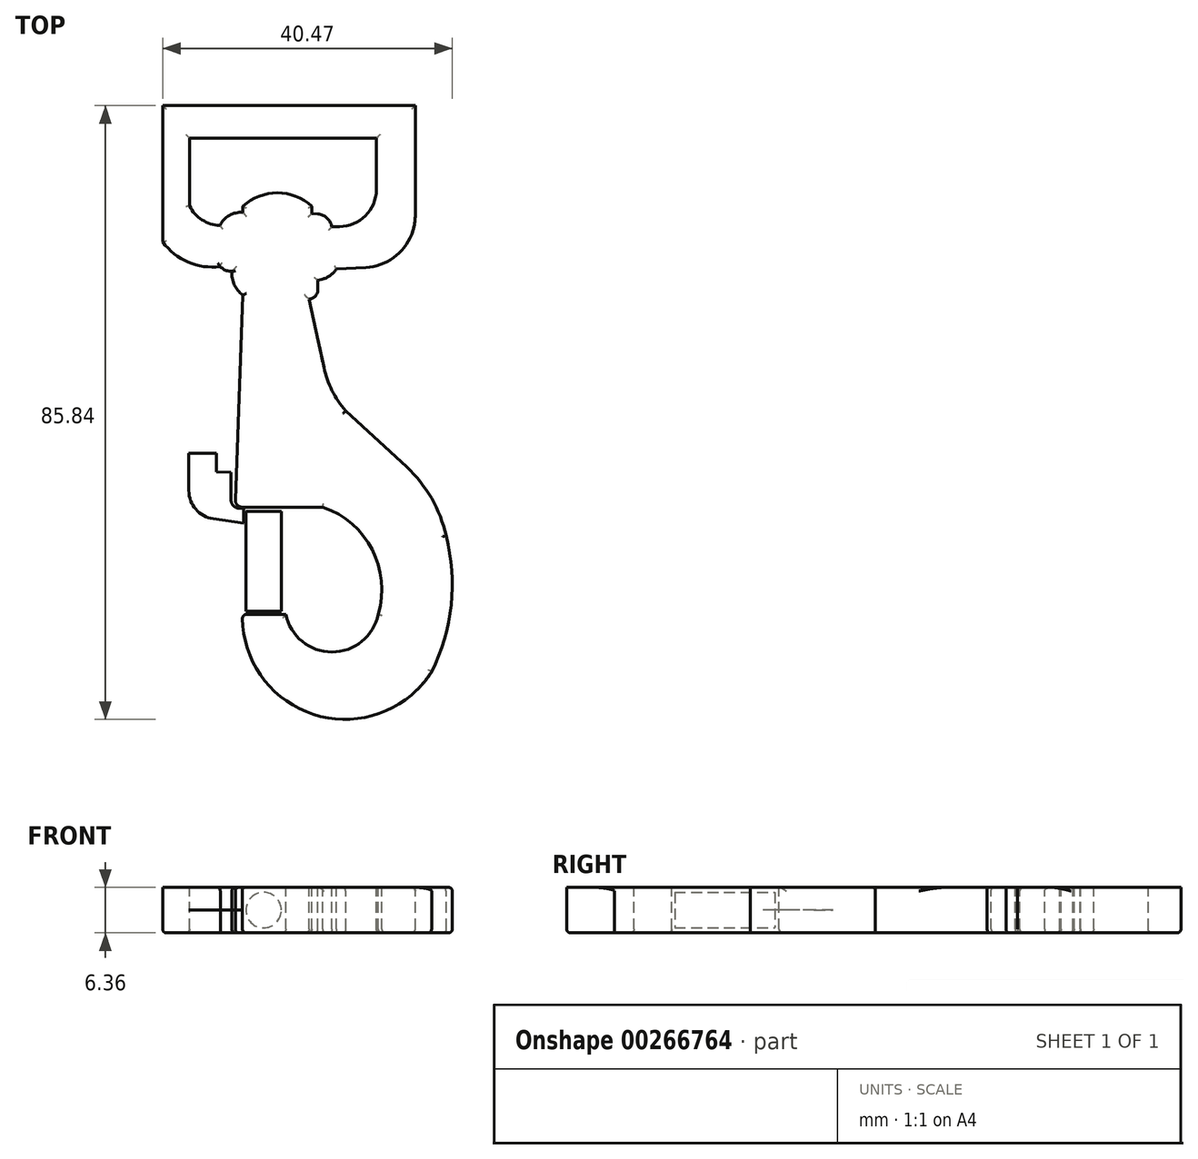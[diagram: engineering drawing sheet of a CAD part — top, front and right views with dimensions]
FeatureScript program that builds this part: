
annotation { "Feature Type Name" : "Feature", "Feature Type Description" : "" }
export const myFeature = defineFeature(function(context is Context, id is Id, definition is map)
    precondition{}
    {
        {
            var Q0;
            Q0=qCreatedBy(makeId("Top.planeOp"),FACE);
            var sketch = newSketch(context, id + "F0", { "sketchPlane" : qUnion([Q0])});
            skLineSegment(sketch, "E0", {"start": v(0, 0) * mm, "end": v(35.3, 0) * mm});
            skLineSegment(sketch, "E1", {"start": v(35.3, 0) * mm, "end": v(35.3, -15.36) * mm});
            skArc(sketch, "E2", {"start": v(28.4, -22.64) * mm, "mid": v(33.3, -20.38) * mm, "end": v(35.3, -15.36) * mm});
            skLineSegment(sketch, "E3", {"start": v(28.4, -22.64) * mm, "end": v(24.3, -22.86) * mm});
            skArc(sketch, "E4", {"start": v(22.26, -24.3) * mm, "mid": v(23.41, -23.76) * mm, "end": v(24.3, -22.86) * mm});
            skLineSegment(sketch, "E5", {"start": v(22.26, -24.3) * mm, "end": v(21.7, -24.44) * mm});
            skLineSegment(sketch, "E6", {"start": v(21.7, -24.44) * mm, "end": v(21.7, -25.7) * mm});
            skArc(sketch, "E7", {"start": v(20.5, -27.08) * mm, "mid": v(21.36, -26.62) * mm, "end": v(21.7, -25.7) * mm});
            skLineSegment(sketch, "E8", {"start": v(20.5, -27.08) * mm, "end": v(22.54, -36.62) * mm});
            skArc(sketch, "E9", {"start": v(22.54, -36.62) * mm, "mid": v(23.67, -39.85) * mm, "end": v(25.58, -42.7) * mm});
            skLineSegment(sketch, "E10", {"start": v(25.58, -42.7) * mm, "end": v(34.09, -50.55) * mm});
            skArc(sketch, "E11", {"start": v(39.62, -60.16) * mm, "mid": v(37.59, -54.93) * mm, "end": v(34.09, -50.55) * mm});
            skArc(sketch, "E12", {"start": v(37.58, -79.19) * mm, "mid": v(40.32, -69.85) * mm, "end": v(39.62, -60.16) * mm});
            skArc(sketch, "E13", {"start": v(11.15, -71.74) * mm, "mid": v(21.6, -85.3) * mm, "end": v(37.58, -79.19) * mm});
            skArc(sketch, "E14", {"start": v(11.74, -71.15) * mm, "mid": v(11.32, -71.32) * mm, "end": v(11.15, -71.74) * mm});
            skLineSegment(sketch, "E15", {"start": v(11.74, -71.15) * mm, "end": v(17.2, -71.15) * mm});
            skArc(sketch, "E16", {"start": v(17.2, -71.15) * mm, "mid": v(23.66, -76.42) * mm, "end": v(30.12, -71.15) * mm});
            skArc(sketch, "E17", {"start": v(30.12, -71.15) * mm, "mid": v(29.28, -62.1) * mm, "end": v(22.4, -56.16) * mm});
            skLineSegment(sketch, "E18", {"start": v(22.4, -56.16) * mm, "end": v(11.12, -56.16) * mm});
            skArc(sketch, "E19", {"start": v(10.17, -55.17) * mm, "mid": v(10.43, -55.87) * mm, "end": v(11.12, -56.16) * mm});
            skLineSegment(sketch, "E20", {"start": v(10.17, -55.17) * mm, "end": v(11.2, -26.51) * mm});
            skArc(sketch, "E21", {"start": v(9.68, -23.18) * mm, "mid": v(10.01, -25.04) * mm, "end": v(11.2, -26.51) * mm});
            skArc(sketch, "E22", {"start": v(8.05, -22.5) * mm, "mid": v(8.8, -23.02) * mm, "end": v(9.68, -23.18) * mm});
            skArc(sketch, "E23", {"start": v(0, -19.06) * mm, "mid": v(3.56, -21.88) * mm, "end": v(8.05, -22.5) * mm});
            skLineSegment(sketch, "E24", {"start": v(0, -19.06) * mm, "end": v(0, 0) * mm});
            skLineSegment(sketch, "E25", {"start": v(9.56, -51.3) * mm, "end": v(7.52, -51.22) * mm});
            skLineSegment(sketch, "E26", {"start": v(7.52, -51.22) * mm, "end": v(7.52, -48.65) * mm});
            skLineSegment(sketch, "E27", {"start": v(7.52, -48.65) * mm, "end": v(3.66, -48.65) * mm});
            skLineSegment(sketch, "E28", {"start": v(3.66, -48.65) * mm, "end": v(3.66, -53.86) * mm});
            skArc(sketch, "E29", {"start": v(3.66, -53.86) * mm, "mid": v(4.63, -56.45) * mm, "end": v(7.07, -57.78) * mm});
            skLineSegment(sketch, "E30", {"start": v(7.07, -57.78) * mm, "end": v(11.35, -58.39) * mm});
            skLineSegment(sketch, "E31", {"start": v(9.56, -51.3) * mm, "end": v(9.56, -55.14) * mm});
            skArc(sketch, "E32", {"start": v(9.56, -55.14) * mm, "mid": v(9.92, -56) * mm, "end": v(10.78, -56.33) * mm});
            skLineSegment(sketch, "E33", {"start": v(10.78, -56.33) * mm, "end": v(11.35, -56.32) * mm});
            skLineSegment(sketch, "E34", {"start": v(11.35, -56.32) * mm, "end": v(11.35, -58.39) * mm});
            skLineSegment(sketch, "E35", {"start": v(3.77, -4.56) * mm, "end": v(29.87, -4.56) * mm});
            skLineSegment(sketch, "E36", {"start": v(29.87, -4.56) * mm, "end": v(29.87, -11.74) * mm});
            skArc(sketch, "E37", {"start": v(24.7, -16.91) * mm, "mid": v(28.36, -15.4) * mm, "end": v(29.87, -11.74) * mm});
            skLineSegment(sketch, "E38", {"start": v(24.7, -16.91) * mm, "end": v(23.65, -16.91) * mm});
            skArc(sketch, "E39", {"start": v(23.65, -16.91) * mm, "mid": v(22.97, -15.71) * mm, "end": v(21.7, -15.16) * mm});
            skLineSegment(sketch, "E40", {"start": v(21.7, -15.16) * mm, "end": v(20.86, -15.08) * mm});
            skLineSegment(sketch, "E41", {"start": v(20.86, -15.08) * mm, "end": v(20.86, -14.1) * mm});
            skArc(sketch, "E42", {"start": v(20.86, -14.1) * mm, "mid": v(16.03, -12.2) * mm, "end": v(11.21, -14.1) * mm});
            skLineSegment(sketch, "E43", {"start": v(11.21, -14.1) * mm, "end": v(11.21, -14.94) * mm});
            skArc(sketch, "E44", {"start": v(11.21, -14.94) * mm, "mid": v(9.33, -15.34) * mm, "end": v(8, -16.74) * mm});
            skArc(sketch, "E45", {"start": v(3.77, -14.02) * mm, "mid": v(5.5, -15.97) * mm, "end": v(8, -16.74) * mm});
            skLineSegment(sketch, "E46", {"start": v(3.77, -4.56) * mm, "end": v(3.77, -14.02) * mm});
            skSolve(sketch);
        }
        {
            var Q0;
            Q0=makeQuery(id+"F0.imprint","IMPRINT",FACE,{"disambiguationData":[TD([[makeQuery(id+"F0.imprint","IMPRINT",EDGE,{"derivedFrom":sQuery(id+"F0.wireOp",EDGE,"E0")}),-1.0]])]});
            extrude(context, id + "F1", {"entities" : qUnion([Q0]), "endBound" : BoundingType.SYMMETRIC, "oppositeDirection" : true, "depth" : 6.35 * mm});
        }
        {
            var Q0;
            Q0=makeQuery(id+"F0.imprint","IMPRINT",FACE,{"disambiguationData":[TD([[makeQuery(id+"F0.imprint","IMPRINT",EDGE,{"derivedFrom":sQuery(id+"F0.wireOp",EDGE,"E25")}),1.0]])]});
            extrude(context, id + "F2", {"entities" : qUnion([Q0]), "oppositeDirection" : true, "depth" : 1 / 203.2 * mm});
        }
        {
            var Q0;
            Q0=qCreatedBy(makeId("Top.planeOp"),FACE);
            var sketch = newSketch(context, id + "F3", { "sketchPlane" : qUnion([Q0])});
            skLineSegment(sketch, "E47.bottom", {"start": v(14.1, -56.78) * mm, "end": v(16.59, -56.78) * mm});
            skLineSegment(sketch, "E47.top", {"start": v(14.1, -70.74) * mm, "end": v(16.59, -70.74) * mm});
            skLineSegment(sketch, "E47.left", {"start": v(14.1, -56.78) * mm, "end": v(14.1, -70.74) * mm});
            skLineSegment(sketch, "E47.right", {"start": v(16.59, -56.78) * mm, "end": v(16.59, -70.74) * mm});
            skSolve(sketch);
        }
        {
            var Q0;
            Q0=makeQuery(id+"F0.imprint","IMPRINT",FACE,{"disambiguationData":[TD([[makeQuery(id+"F0.imprint","IMPRINT",EDGE,{"derivedFrom":sQuery(id+"F0.wireOp",EDGE,"E35")}),-1.0]])]});
            extrude(context, id + "F4", {"entities" : qUnion([Q0]), "operationType" : NewBodyOperationType.REMOVE, "oppositeDirection" : true, "depth" : 25.4 * mm});
        }
        {
            var Q0;
            Q0=makeQuery(id+"F1.opExtrude","CAP_EDGE",EDGE,{"disambiguationData":[OSD([sQuery(id+"F0.wireOp",EDGE,"E20")])],"isStart":true});
            var Q1;
            Q1=makeQuery(id+"F1.opExtrude","CAP_EDGE",EDGE,{"disambiguationData":[OSD([sQuery(id+"F0.wireOp",EDGE,"E21")])],"isStart":true});
            var Q2;
            Q2=makeQuery(id+"F1.opExtrude","CAP_EDGE",EDGE,{"disambiguationData":[OSD([sQuery(id+"F0.wireOp",EDGE,"E22")])],"isStart":false});
            var Q3;
            Q3=makeQuery(id+"F1.opExtrude","CAP_EDGE",EDGE,{"disambiguationData":[OSD([sQuery(id+"F0.wireOp",EDGE,"E23")])],"isStart":true});
            var Q4;
            Q4=makeQuery(id+"F1.opExtrude","CAP_EDGE",EDGE,{"disambiguationData":[OSD([sQuery(id+"F0.wireOp",EDGE,"E9")])],"isStart":true});
            var Q5;
            Q5=makeQuery(id+"F1.opExtrude","CAP_EDGE",EDGE,{"disambiguationData":[OSD([sQuery(id+"F0.wireOp",EDGE,"E10")])],"isStart":true});
            var Q6;
            Q6=makeQuery(id+"F1.opExtrude","CAP_EDGE",EDGE,{"disambiguationData":[OSD([sQuery(id+"F0.wireOp",EDGE,"E11")])],"isStart":true});
            var Q7;
            Q7=makeQuery(id+"F1.opExtrude","CAP_EDGE",EDGE,{"disambiguationData":[OSD([sQuery(id+"F0.wireOp",EDGE,"E12")])],"isStart":true});
            var Q8;
            Q8=makeQuery(id+"F1.opExtrude","CAP_FACE",FACE,{"disambiguationData":[OSD([sQuery(id+"F0.wireOp",EDGE,"E0"),sQuery(id+"F0.wireOp",EDGE,"E1"),sQuery(id+"F0.wireOp",EDGE,"E2"),sQuery(id+"F0.wireOp",EDGE,"E3"),sQuery(id+"F0.wireOp",EDGE,"E4"),sQuery(id+"F0.wireOp",EDGE,"E5"),sQuery(id+"F0.wireOp",EDGE,"E6"),sQuery(id+"F0.wireOp",EDGE,"E7"),sQuery(id+"F0.wireOp",EDGE,"E8"),sQuery(id+"F0.wireOp",EDGE,"E9"),sQuery(id+"F0.wireOp",EDGE,"E10"),sQuery(id+"F0.wireOp",EDGE,"E11"),sQuery(id+"F0.wireOp",EDGE,"E12"),sQuery(id+"F0.wireOp",EDGE,"E13"),sQuery(id+"F0.wireOp",EDGE,"E14"),sQuery(id+"F0.wireOp",EDGE,"E15"),sQuery(id+"F0.wireOp",EDGE,"E16"),sQuery(id+"F0.wireOp",EDGE,"E17"),sQuery(id+"F0.wireOp",EDGE,"E18"),sQuery(id+"F0.wireOp",EDGE,"E19"),sQuery(id+"F0.wireOp",EDGE,"E20"),sQuery(id+"F0.wireOp",EDGE,"E21"),sQuery(id+"F0.wireOp",EDGE,"E22"),sQuery(id+"F0.wireOp",EDGE,"E23"),sQuery(id+"F0.wireOp",EDGE,"E24"),sQuery(id+"F0.wireOp",EDGE,"E35"),sQuery(id+"F0.wireOp",EDGE,"E36"),sQuery(id+"F0.wireOp",EDGE,"E37"),sQuery(id+"F0.wireOp",EDGE,"E38"),sQuery(id+"F0.wireOp",EDGE,"E39"),sQuery(id+"F0.wireOp",EDGE,"E40"),sQuery(id+"F0.wireOp",EDGE,"E41"),sQuery(id+"F0.wireOp",EDGE,"E42"),sQuery(id+"F0.wireOp",EDGE,"E43"),sQuery(id+"F0.wireOp",EDGE,"E44"),sQuery(id+"F0.wireOp",EDGE,"E45"),sQuery(id+"F0.wireOp",EDGE,"E46")])],"isStart":false});
            var Q9;
            Q9=makeQuery(id+"F1.opExtrude","CAP_EDGE",EDGE,{"disambiguationData":[OSD([sQuery(id+"F0.wireOp",EDGE,"E1")])],"isStart":true});
            fillet(context, id + "F5", {"entities" : qUnion([Q0, Q1, Q2, Q3, Q4, Q5, Q6, Q7, Q8, Q9]), "radius" : 0.5 * mm, "allowEdgeOverflow" : false});
        }
        {
            var Q0;
            Q0=makeQuery(id+"F3.imprint","IMPRINT",FACE,{"disambiguationData":[TD([[makeQuery(id+"F3.imprint","IMPRINT",EDGE,{"derivedFrom":sQuery(id+"F3.wireOp",EDGE,"E47.bottom")}),-1.0]])]});
            var Q1;
            Q1=sQuery(id+"F3.wireOp",EDGE,"E47.left");
            revolve(context, id + "F6", {"entities" : qUnion([Q0]), "axis" : qUnion([Q1]), "revolveType" : RevolveType.FULL});
        }
    });
